# Revit family: BVS.SAT
name_source: partatom
category: Plumbing Fixtures
revit_build: Autodesk Revit MEP 2016 (Build: 20150220_1215(x64)
units: mm (PartAtom-declared; Revit-internal decimal feet)

## family parameters
Cut with Voids When Loaded = No
Host = Face
OmniClass Number = 23.45.05.14.99
OmniClass Title = Other Sanitary Washing Plumbing Fixtures
Part Type = Normal
Room Calculation Point = No
Round Connector Dimension = Use Diameter
Shared = Yes

## types (1)
- BVS-2
    Assembly Code = D2020
    BVS -Brass Ball Valve Shut-off, .75 NPT Inlets & Outlet Connections For ET71-2 = Yes
    CW Connection = Yes
    CWFU = 0
    Default Elevation = 0"
    Description = Brass Ball Valve Shut-off, .75 NPT Inlets & Outlet Connections For ET71-2
    HW Connection = Yes
    HWFU = 0
    Manufacturer = Acorn Controls
    Material = Default
    Model = BVS-2
    Revised Date = 09/17/19
    Tempered Water Connection = Yes
    URL = http://www.acorneng.com
    Vent Connection = No
    WFU = 0
    Waste Connection = No

## geometry (parser evidence)
native form markers: Sweep x5
no freeform markers — native parametric forms only
